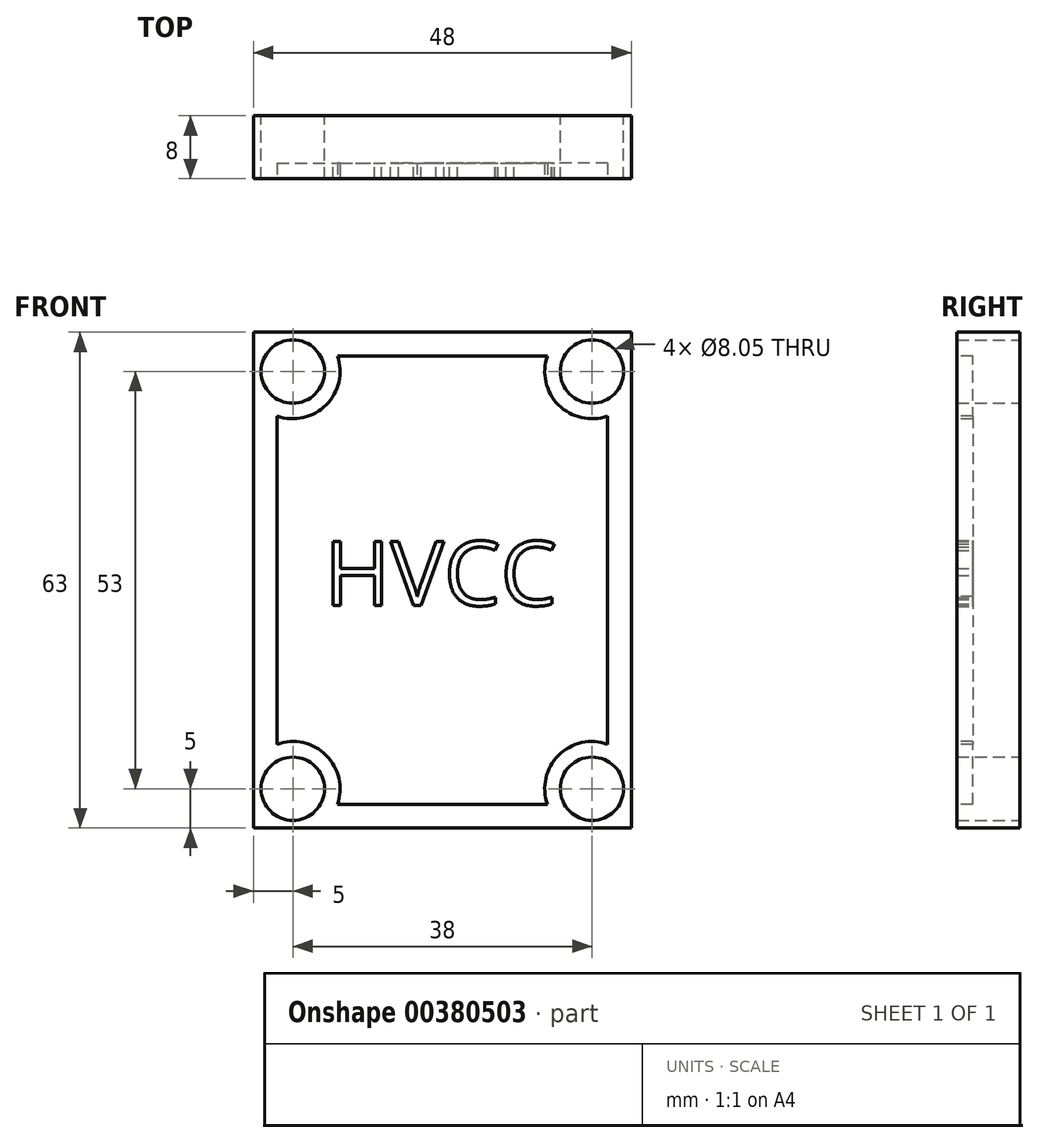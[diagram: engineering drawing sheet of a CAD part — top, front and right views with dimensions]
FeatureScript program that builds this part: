
annotation { "Feature Type Name" : "Feature", "Feature Type Description" : "" }
export const myFeature = defineFeature(function(context is Context, id is Id, definition is map)
    precondition{}
    {
        {
            var Q0;
            Q0=qCreatedBy(makeId("Front.planeOp"),FACE);
            var sketch = newSketch(context, id + "F0", { "sketchPlane" : qUnion([Q0])});
            skLineSegment(sketch, "E0.bottom", {"start": v(0, 0) * mm, "end": v(-48, 0) * mm});
            skLineSegment(sketch, "E0.top", {"start": v(0, -63) * mm, "end": v(-48, -63) * mm});
            skLineSegment(sketch, "E0.left", {"start": v(0, 0) * mm, "end": v(0, -63) * mm});
            skLineSegment(sketch, "E0.right", {"start": v(-48, 0) * mm, "end": v(-48, -63) * mm});
            skCircle(sketch, "E1", {"center": v(-43, -5) * mm, "radius": 4.03 * mm});
            skCircle(sketch, "E2", {"center": v(-5, -5) * mm, "radius": 4.03 * mm});
            skCircle(sketch, "E3", {"center": v(-43, -58) * mm, "radius": 4.03 * mm});
            skCircle(sketch, "E4", {"center": v(-5, -58) * mm, "radius": 4.03 * mm});
            skLineSegment(sketch, "E5", {"start": v(-45, -13) * mm, "end": v(-45, -50) * mm});
            skLineSegment(sketch, "E6", {"start": v(-43, -52) * mm, "end": v(-43, -52) * mm});
            skLineSegment(sketch, "E7", {"start": v(-37, -58) * mm, "end": v(-37, -58) * mm});
            skLineSegment(sketch, "E8", {"start": v(-35, -60) * mm, "end": v(-13, -60) * mm});
            skLineSegment(sketch, "E9", {"start": v(-11, -58) * mm, "end": v(-11, -58) * mm});
            skLineSegment(sketch, "E10", {"start": v(-5, -52) * mm, "end": v(-5, -52) * mm});
            skLineSegment(sketch, "E11", {"start": v(-3, -50) * mm, "end": v(-3, -13) * mm});
            skLineSegment(sketch, "E12", {"start": v(-5, -11) * mm, "end": v(-5, -11) * mm});
            skLineSegment(sketch, "E13", {"start": v(-11, -5) * mm, "end": v(-11, -5) * mm});
            skLineSegment(sketch, "E14", {"start": v(-13, -3) * mm, "end": v(-35, -3) * mm});
            skLineSegment(sketch, "E15", {"start": v(-37, -5) * mm, "end": v(-37, -5) * mm});
            skLineSegment(sketch, "E16", {"start": v(-43, -11) * mm, "end": v(-43, -11) * mm});
            skLineSegment(sketch, "E17", {"start": v(-24, 0) * mm, "end": v(-24, -63) * mm, "construction": true});
            skLineSegment(sketch, "E18", {"start": v(-48, -31.5) * mm, "end": v(0, -31.5) * mm, "construction": true});
            skPoint(sketch, "E19.visualSharp", {"position": v(-37, -11) * mm});
            skArc(sketch, "E20.filletArc", {"start": v(-43, -11) * mm, "mid": v(-38.76, -9.24) * mm, "end": v(-37, -5) * mm});
            skPoint(sketch, "E21.visualSharp", {"position": v(-37, -3) * mm});
            skArc(sketch, "E21.filletArc", {"start": v(-35, -3) * mm, "mid": v(-36.41, -3.59) * mm, "end": v(-37, -5) * mm});
            skPoint(sketch, "E22.visualSharp", {"position": v(-45, -11) * mm});
            skArc(sketch, "E22.filletArc", {"start": v(-43, -11) * mm, "mid": v(-44.41, -11.59) * mm, "end": v(-45, -13) * mm});
            skPoint(sketch, "E23.visualSharp", {"position": v(-11, -11) * mm});
            skArc(sketch, "E23.filletArc", {"start": v(-11, -5) * mm, "mid": v(-9.24, -9.24) * mm, "end": v(-5, -11) * mm});
            skPoint(sketch, "E24.visualSharp", {"position": v(-11, -52) * mm});
            skArc(sketch, "E24.filletArc", {"start": v(-5, -52) * mm, "mid": v(-9.24, -53.76) * mm, "end": v(-11, -58) * mm});
            skPoint(sketch, "E25.visualSharp", {"position": v(-37, -52) * mm});
            skArc(sketch, "E25.filletArc", {"start": v(-37, -58) * mm, "mid": v(-38.76, -53.76) * mm, "end": v(-43, -52) * mm});
            skPoint(sketch, "E26.visualSharp", {"position": v(-11, -3) * mm});
            skArc(sketch, "E26.filletArc", {"start": v(-11, -5) * mm, "mid": v(-11.59, -3.59) * mm, "end": v(-13, -3) * mm});
            skPoint(sketch, "E27.visualSharp", {"position": v(-3, -11) * mm});
            skArc(sketch, "E27.filletArc", {"start": v(-3, -13) * mm, "mid": v(-3.59, -11.59) * mm, "end": v(-5, -11) * mm});
            skPoint(sketch, "E28.visualSharp", {"position": v(-3, -52) * mm});
            skArc(sketch, "E28.filletArc", {"start": v(-5, -52) * mm, "mid": v(-3.59, -51.41) * mm, "end": v(-3, -50) * mm});
            skPoint(sketch, "E29.visualSharp", {"position": v(-11, -60) * mm});
            skArc(sketch, "E29.filletArc", {"start": v(-13, -60) * mm, "mid": v(-11.59, -59.41) * mm, "end": v(-11, -58) * mm});
            skPoint(sketch, "E30.visualSharp", {"position": v(-37, -60) * mm});
            skArc(sketch, "E30.filletArc", {"start": v(-37, -58) * mm, "mid": v(-36.41, -59.41) * mm, "end": v(-35, -60) * mm});
            skPoint(sketch, "E31.visualSharp", {"position": v(-45, -52) * mm});
            skArc(sketch, "E31.filletArc", {"start": v(-45, -50) * mm, "mid": v(-44.41, -51.41) * mm, "end": v(-43, -52) * mm});
            skText(sketch, "E32", { "text": "HVCC", "fontName": "OpenSans-Regular.ttf"});
            const initialGuessF0  = {"E32": [-0.039, -0.03471, 1, 0, 0.00821]};
            skSetInitialGuess(sketch, initialGuessF0);
            skSolve(sketch);
        }
        {
            var Q0;
            Q0=makeQuery(id+"F0.imprint","IMPRINT",FACE,{"disambiguationData":[TD([[makeQuery(id+"F0.imprint","IMPRINT",EDGE,{"derivedFrom":sQuery(id+"F0.wireOp",EDGE,"E32.sketch_text.stroke-0")}),-1.0]])]});
            var Q1;
            Q1=makeQuery(id+"F0.imprint","IMPRINT",FACE,{"disambiguationData":[TD([[makeQuery(id+"F0.imprint","IMPRINT",EDGE,{"derivedFrom":sQuery(id+"F0.wireOp",EDGE,"E32.sketch_text.stroke-12")}),-1.0]])]});
            var Q2;
            Q2=makeQuery(id+"F0.imprint","IMPRINT",FACE,{"disambiguationData":[TD([[makeQuery(id+"F0.imprint","IMPRINT",EDGE,{"derivedFrom":sQuery(id+"F0.wireOp",EDGE,"E32.sketch_text.stroke-21")}),-1.0]])]});
            var Q3;
            Q3=makeQuery(id+"F0.imprint","IMPRINT",FACE,{"disambiguationData":[TD([[makeQuery(id+"F0.imprint","IMPRINT",EDGE,{"derivedFrom":sQuery(id+"F0.wireOp",EDGE,"E32.sketch_text.stroke-36")}),-1.0]])]});
            var Q4;
            Q4=makeQuery(id+"F0.imprint","IMPRINT",FACE,{"disambiguationData":[TD([[makeQuery(id+"F0.imprint","IMPRINT",EDGE,{"derivedFrom":sQuery(id+"F0.wireOp",EDGE,"E5")}),1.0]])]});
            var Q5;
            Q5=makeQuery(id+"F0.imprint","IMPRINT",FACE,{"disambiguationData":[TD([[makeQuery(id+"F0.imprint","IMPRINT",EDGE,{"derivedFrom":sQuery(id+"F0.wireOp",EDGE,"E0.bottom")}),1.0]])]});
            extrude(context, id + "F1", {"entities" : qUnion([Q0, Q1, Q2, Q3, Q4, Q5]), "depth" : 8 * mm});
        }
        {
            var Q0;
            Q0=makeQuery(id+"F1.opExtrude","CAP_FACE",FACE,{"disambiguationData":[OSD([sQuery(id+"F0.wireOp",EDGE,"E0.bottom"),sQuery(id+"F0.wireOp",EDGE,"E0.top"),sQuery(id+"F0.wireOp",EDGE,"E0.left"),sQuery(id+"F0.wireOp",EDGE,"E0.right"),sQuery(id+"F0.wireOp",EDGE,"E1"),sQuery(id+"F0.wireOp",EDGE,"E2"),sQuery(id+"F0.wireOp",EDGE,"E3"),sQuery(id+"F0.wireOp",EDGE,"E4")])],"isStart":false});
            var sketch = newSketch(context, id + "F2", { "sketchPlane" : qUnion([Q0])});
            skArc(sketch, "E33.0", {"start": v(-45, -10.66) * mm, "mid": v(-38.76, -9.24) * mm, "end": v(-37.34, -3) * mm});
            skLineSegment(sketch, "E33.1", {"start": v(-10.66, -3) * mm, "end": v(-37.34, -3) * mm});
            skLineSegment(sketch, "E33.2", {"start": v(-45, -10.66) * mm, "end": v(-45, -52.34) * mm});
            skArc(sketch, "E33.3", {"start": v(-10.66, -3) * mm, "mid": v(-9.24, -9.24) * mm, "end": v(-3, -10.66) * mm});
            skArc(sketch, "E33.4", {"start": v(-37.34, -60) * mm, "mid": v(-38.76, -53.76) * mm, "end": v(-45, -52.34) * mm});
            skLineSegment(sketch, "E33.5", {"start": v(-37.34, -60) * mm, "end": v(-10.66, -60) * mm});
            skArc(sketch, "E33.6", {"start": v(-3, -52.34) * mm, "mid": v(-9.24, -53.76) * mm, "end": v(-10.66, -60) * mm});
            skLineSegment(sketch, "E33.7", {"start": v(-3, -52.34) * mm, "end": v(-3, -10.66) * mm});
            skSolve(sketch);
        }
        {
            var Q0;
            Q0=qSketchRegion(id+"F2",true);
            extrude(context, id + "F3", {"entities" : qUnion([Q0]), "operationType" : NewBodyOperationType.REMOVE, "oppositeDirection" : true, "depth" : 2 * mm});
        }
        {
            var Q0;
            Q0=makeQuery(id+"F0.imprint","IMPRINT",FACE,{"disambiguationData":[TD([[makeQuery(id+"F0.imprint","IMPRINT",EDGE,{"derivedFrom":sQuery(id+"F0.wireOp",EDGE,"E32.sketch_text.stroke-36")}),-1.0]])]});
            var Q1;
            Q1=makeQuery(id+"F0.imprint","IMPRINT",FACE,{"disambiguationData":[TD([[makeQuery(id+"F0.imprint","IMPRINT",EDGE,{"derivedFrom":sQuery(id+"F0.wireOp",EDGE,"E32.sketch_text.stroke-21")}),-1.0]])]});
            var Q2;
            Q2=makeQuery(id+"F0.imprint","IMPRINT",FACE,{"disambiguationData":[TD([[makeQuery(id+"F0.imprint","IMPRINT",EDGE,{"derivedFrom":sQuery(id+"F0.wireOp",EDGE,"E32.sketch_text.stroke-12")}),-1.0]])]});
            var Q3;
            Q3=makeQuery(id+"F0.imprint","IMPRINT",FACE,{"disambiguationData":[TD([[makeQuery(id+"F0.imprint","IMPRINT",EDGE,{"derivedFrom":sQuery(id+"F0.wireOp",EDGE,"E32.sketch_text.stroke-0")}),-1.0]])]});
            extrude(context, id + "F4", {"entities" : qUnion([Q0, Q1, Q2, Q3]), "operationType" : NewBodyOperationType.ADD, "depth" : 8 * mm});
        }
    });
